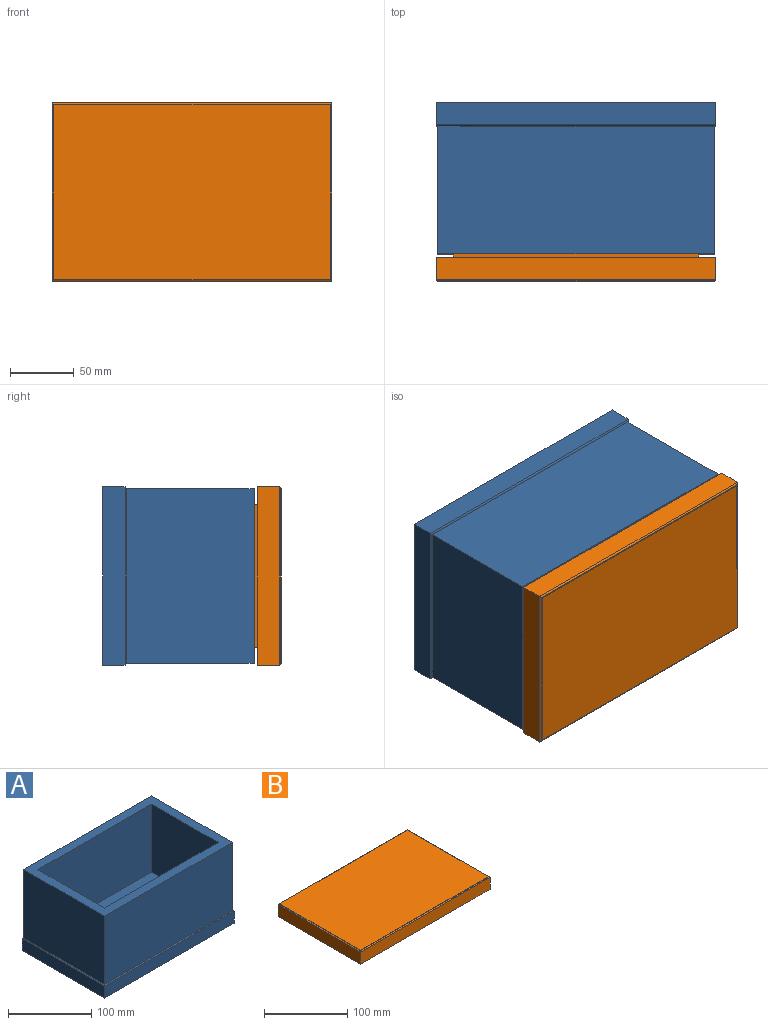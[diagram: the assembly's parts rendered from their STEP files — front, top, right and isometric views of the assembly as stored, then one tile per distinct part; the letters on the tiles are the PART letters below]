
ASSEMBLY  parts=2 mates=1
PART A: 27 faces, bbox 220x140x119 mm
  f0: plane 220x17.6mm, normal (0,1,0), area 3872mm2, adj f7,f8,f10,f15
  f1: plane 137x100.5mm, normal (-1,0,0), area 13768.5mm2, adj f2,f5,f16,f25
  f2: cylinder r=1.5mm len=140mm, axis (0,-1,0), area 259mm2, adj f1,f6,f8,f12,f15,f18
  f3: cylinder r=1.5mm len=140mm, axis (0,1,0), area 259mm2, adj f4,f6,f7,f14,f15,f17
  f4: plane 137x100.5mm, normal (1,0,0), area 13768.5mm2, adj f3,f5,f16,f25
  f5: plane 217x100.5mm, normal (0,-1,0), area 21808.5mm2, adj f1,f4,f6,f25
  f6: cylinder r=1.5mm len=220mm, axis (1,0,0), area 408.4mm2, adj f2,f3,f5,f9,f11,f13
  f7: plane 140x17.6mm, normal (1,0,0), area 2464mm2, adj f0,f3,f9,f10
  f8: plane 140x17.6mm, normal (-1,0,0), area 2464mm2, adj f0,f2,f9,f10
  f9: plane 220x17.6mm, normal (0,-1,0), area 3872mm2, adj f6,f7,f8,f10
  f10: plane 220x140mm, normal (0,0,-1), area 30800mm2, adj f0,f7,f8,f9
  f11: cylinder r=1.5mm len=0.25mm, axis (0,-1,0), area 0mm2, adj f6,f12
  f12: cylinder r=1.5mm len=0.25mm, axis (1,0,0), area 0mm2, adj f2,f11
  f13: cylinder r=1.5mm len=0.25mm, axis (0,1,0), area 0mm2, adj f6,f14
  f14: cylinder r=1.5mm len=0.25mm, axis (1,0,0), area 0mm2, adj f3,f13
  f15: cylinder r=1.5mm len=220mm, axis (-1,0,0), area 408.4mm2, adj f0,f2,f3,f16,f19,f20
  f16: plane 217x100.5mm, normal (0,1,0), area 21808.5mm2, adj f1,f4,f15,f25
  f17: cylinder r=1.5mm len=0.25mm, axis (-1,0,0), area 0mm2, adj f3,f20
  f18: cylinder r=1.5mm len=0.25mm, axis (-1,0,0), area 0mm2, adj f2,f19
  f19: cylinder r=1.5mm len=0.25mm, axis (0,-1,0), area 0mm2, adj f15,f18
  f20: cylinder r=1.5mm len=0.25mm, axis (0,1,0), area 0mm2, adj f15,f17
  f21: plane 193x100mm, normal (0,-1,0), area 19300mm2, adj f22,f24,f25,f26
  f22: plane 113x100mm, normal (-1,0,0), area 11300mm2, adj f21,f23,f25,f26
  f23: plane 193x100mm, normal (0,1,0), area 19300mm2, adj f22,f24,f25,f26
  f24: plane 113x100mm, normal (1,0,0), area 11300mm2, adj f21,f23,f25,f26
  f25: plane 217x137mm, normal (0,0,1), area 7920mm2, adj f1,f4,f5,f16,f21,f22,f23,f24
  f26: plane 193x113mm, normal (0,0,1), area 21809mm2, adj f21,f22,f23,f24
PART B: 35 faces, bbox 220x140x24 mm
  f0: cylinder r=1.4mm len=140mm, axis (0,1,0), area 262mm2, adj f4,f6,f17,f18,f19,f25,f33,f34
  f1: cylinder r=1.4mm len=140mm, axis (0,-1,0), area 262mm2, adj f4,f5,f22,f23,f24,f25,f29,f30
  f2: plane 217x137mm, normal (0,0,1), area 29729mm2, adj f3,f17,f22,f26
  f3: plane 217x0.5mm, normal (0,1,0), area 108.5mm2, adj f2,f4,f17,f22
  f4: cylinder r=1.4mm len=220mm, axis (1,0,0), area 413.2mm2, adj f0,f1,f3,f8,f15,f16,f20,f21
  f5: plane 140x17.6mm, normal (-1,0,0), area 2464mm2, adj f1,f7,f8,f9
  f6: plane 140x17.6mm, normal (1,0,0), area 2464mm2, adj f0,f7,f8,f9
  f7: plane 220x17.6mm, normal (0,-1,0), area 3872mm2, adj f5,f6,f9,f25
  f8: plane 220x17.6mm, normal (0,1,0), area 3872mm2, adj f4,f5,f6,f9
  f9: plane 220x140mm, normal (0,0,-1), area 8991mm2, adj f5,f6,f7,f8,f10,f11,f12,f13
  f10: plane 193x5mm, normal (0,-1,0), area 965mm2, adj f9,f11,f13,f14
  f11: plane 113x5mm, normal (-1,0,0), area 565mm2, adj f9,f10,f12,f14
  f12: plane 193x5mm, normal (0,1,0), area 965mm2, adj f9,f11,f13,f14
  f13: plane 113x5mm, normal (1,0,0), area 565mm2, adj f9,f10,f12,f14
  f14: plane 193x113mm, normal (0,0,-1), area 21809mm2, adj f10,f11,f12,f13
  f15: plane 0.38x0.01mm, normal (1,0,0), area 0mm2, adj f4,f16
  f16: cylinder r=1.4mm len=0.38mm, axis (0,1,0), area 0mm2, adj f4,f15,f18
  f17: plane 137x0.5mm, normal (1,0,0), area 68.5mm2, adj f0,f2,f3,f26
  f18: cylinder r=1.4mm len=0.38mm, axis (1,0,0), area 0mm2, adj f0,f16,f19
  f19: plane 0.38x0.01mm, normal (0,1,0), area 0mm2, adj f0,f18
  f20: cylinder r=1.4mm len=0.38mm, axis (0,-1,0), area 0mm2, adj f4,f21,f23
  f21: plane 0.38x0.01mm, normal (-1,0,0), area 0mm2, adj f4,f20
  f22: plane 137x0.5mm, normal (-1,0,0), area 68.5mm2, adj f1,f2,f3,f26
  f23: cylinder r=1.4mm len=0.38mm, axis (1,0,0), area 0mm2, adj f1,f20,f24
  f24: plane 0.38x0.01mm, normal (0,1,0), area 0mm2, adj f1,f23
  f25: cylinder r=1.4mm len=220mm, axis (-1,0,0), area 413.2mm2, adj f0,f1,f7,f26,f27,f28,f31,f32
  f26: plane 217x0.5mm, normal (0,-1,0), area 108.5mm2, adj f2,f17,f22,f25
  f27: cylinder r=1.4mm len=0.38mm, axis (0,-1,0), area 0mm2, adj f25,f28,f29
  f28: plane 0.38x0.01mm, normal (-1,0,0), area 0mm2, adj f25,f27
  f29: cylinder r=1.4mm len=0.38mm, axis (-1,0,0), area 0mm2, adj f1,f27,f30
  f30: plane 0.38x0.01mm, normal (0,-1,0), area 0mm2, adj f1,f29
  f31: plane 0.38x0.01mm, normal (1,0,0), area 0mm2, adj f25,f32
  f32: cylinder r=1.4mm len=0.38mm, axis (0,1,0), area 0mm2, adj f25,f31,f34
  f33: plane 0.38x0.01mm, normal (0,-1,0), area 0mm2, adj f0,f34
  f34: cylinder r=1.4mm len=0.38mm, axis (-1,0,0), area 0mm2, adj f0,f32,f33
PLACE A rot(axis=(1,0,0),90deg) t=(130.05,82.46,160.21)mm
PLACE B rot(axis=(0,0.71,-0.71),180deg) t=(222.94,-39.04,184.06)mm
MATE fastened B.f10 <-> A.f21  axis (0,0,1) through (179.01,-36.54,239.38)mm
